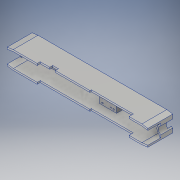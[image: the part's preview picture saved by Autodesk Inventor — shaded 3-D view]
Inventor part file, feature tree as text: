
AUTODESK INVENTOR PART (.ipt)
format: ipt  version: 2017 (Build 210142000, 142)  size: 501,248 bytes
history: native  units: in
note: dims shown in document units (in); Inventor stores cm internally (conversion verified against a paired STEP export)
features: projected_geometry x21, sketch x16, extrude x12, hole x5, reference x4, other x4, chamfer x1
ambient origin geometry x8: Origin, YZ Plane, XZ Plane, XY Plane, X Axis, Y Axis, Z Axis, Center Point
bodies: Solid1 (feature_tree)
feature tree (63):
  extrude  "Extrusion1"  Depth=6.4567in
  extrude  "Extrusion2"  Depth=0.2756in
  extrude  "Extrusion3"  Depth=0.0787in
  extrude  "Extrusion4"  Depth=0.1181in
  extrude  "Extrusion5"  Depth=0.0591in
  hole  "Hole1"  [1 undecoded]
  extrude  "Extrusion6"  Depth=0.0591in
  extrude  "Extrusion7"  Depth=0.7874in
  extrude  "Extrusion8"  Depth=0.2953in TaperAngle=0.0deg
  chamfer  "Chamfer1"  Distance=0.2953in
  hole  "Hole2"  [1 undecoded]
  extrude  "Extrusion9"  Depth=0.1378in
  hole  "Hole3"  [1 undecoded]
  extrude  "Extrusion10"  Depth=0.5118in
  extrude  "Extrusion11"  Depth=0.0591in
  hole  "Hole4"  [1 undecoded]
  extrude  "Extrusion12"  Depth=0.1378in
  hole  "Hole5"  [1 undecoded]
  sketch  "Sketch1"  dims[d0=0.8268in d1=6.4567in]
  sketch  "Sketch2"  dims[d2=1.1417in d3=0.0in d4=0.2756in]
  projected_geometry  "Projected Loop1"
  sketch  "Sketch3"  dims[d5=0.0394in d6=0.0787in]
  sketch  "Sketch4"  dims[d7=0.5906in d8=0.0in d9=0.1181in d10=0.3543in]
  projected_geometry  "Projected Loop2"
  projected_geometry  "Projected Loop3"
  projected_geometry  "Projected Loop4"
  projected_geometry  "Projected Loop5"
  sketch  "Sketch5"  dims[d11=0.1181in d12=0.0591in]
  projected_geometry  "Projected Loop6"
  projected_geometry  "Projected Loop7"
  projected_geometry  "Projected Loop8"
  projected_geometry  "Projected Loop9"
  projected_geometry  "Projected Loop10"
  sketch  "Sketch7"  dims[d13=0.0591in d14=0.0591in]
  projected_geometry  "Projected Loop11"
  sketch  "Sketch8"  dims[d15=0.0591in d16=0.0591in]
  sketch  "Sketch9"  dims[d17=0.0591in d18=0.7874in]
  projected_geometry  "Projected Loop13"
  sketch  "Sketch10"  dims[d19=2.0276in d20=0.2953in d21=0.0in]
  projected_geometry  "Projected Loop14"
  projected_geometry  "Projected Loop15"
  sketch  "Sketch11"  dims[d22=0.2559in]
  projected_geometry  "Projected Loop16"
  sketch  "Sketch12"  dims[d23=0.2953in]
  projected_geometry  "Projected Loop17"
  sketch  "Sketch13"  dims[d24=0.4331in]
  projected_geometry  "Projected Loop18"
  projected_geometry  "Projected Loop19"
  sketch  "Sketch14"  dims[d25=0.9449in]
  projected_geometry  "Projected Loop20"
  projected_geometry  "Projected Loop21"
  sketch  "Sketch15"  dims[d26=0.0787in]
  reference  "Reference1"
  reference  "Reference2"
  sketch  "Sketch16"  dims[d27=0.0787in]
  projected_geometry  "Projected Loop22"
  sketch  "Sketch17"  dims[d28=0.8705in d29=0.2953in d30=0.0in d31=0.1772in d32=0.0in d33=0.1378in d36=0.4921in d37=0.5118in d39=0.063in d40=0.2362in d41=0.1575in d42=0.0787in d43=90.0deg d44=0.315in d45=0.8108in d46=0.0591in d47=0.0591in d48=0.1378in d49=0.3543in d50=0.3937in d51=0.3543in d52=0.2362in d53=0.0551in d54=0.0in d55=0.1378in d56=0.1378in d57=0.6496in d58=0.0622in d59=0.0in d60=0.0591in d61=0.0591in d62=0.0in d63=0.0591in d64=0.0787in d65=45.0deg d66=0.063in d67=0.2362in d68=0.1575in d69=0.0787in d70=90.0deg d71=0.315in d72=0.8108in d73=0.1772in d74=0.0315in d75=0.0in d77=0.6496in d78=0.4921in d79=0.063in d80=0.2362in d81=0.1575in d82=0.0787in d83=90.0deg d84=0.315in d85=0.8108in d86=0.4331in d87=0.2598in d88=0.2756in d89=0.0394in d90=0.0in d91=4.2126in d92=1.378in d93=0.1378in d94=0.1969in d95=1.9291in d96=0.0394in d97=0.0in d98=0.0433in d99=0.2362in d100=0.1575in d101=0.0787in d102=90.0deg d103=0.315in d104=0.8108in d105=0.6339in d106=0.0591in d107=0.315in d108=0.0in d109=0.0433in d110=0.2362in d111=0.1575in d112=0.0787in d113=90.0deg d114=0.315in d115=0.8108in]
  reference  "Reference3"
  reference  "Reference4"
  other  "<userpath>\Dropbox\Work\HeadSLAM\xtion_internal.iam"
  other  "xtion_internal.iam"
  other  "xtion_ir_cam:1"
  other  "xtion_rgb_cam:1"
note: 5 required parameter values undecoded (feature->parameter linkage not recoverable at this tier; creation-order binding heuristic only, values carry confidence <= 0.55)
